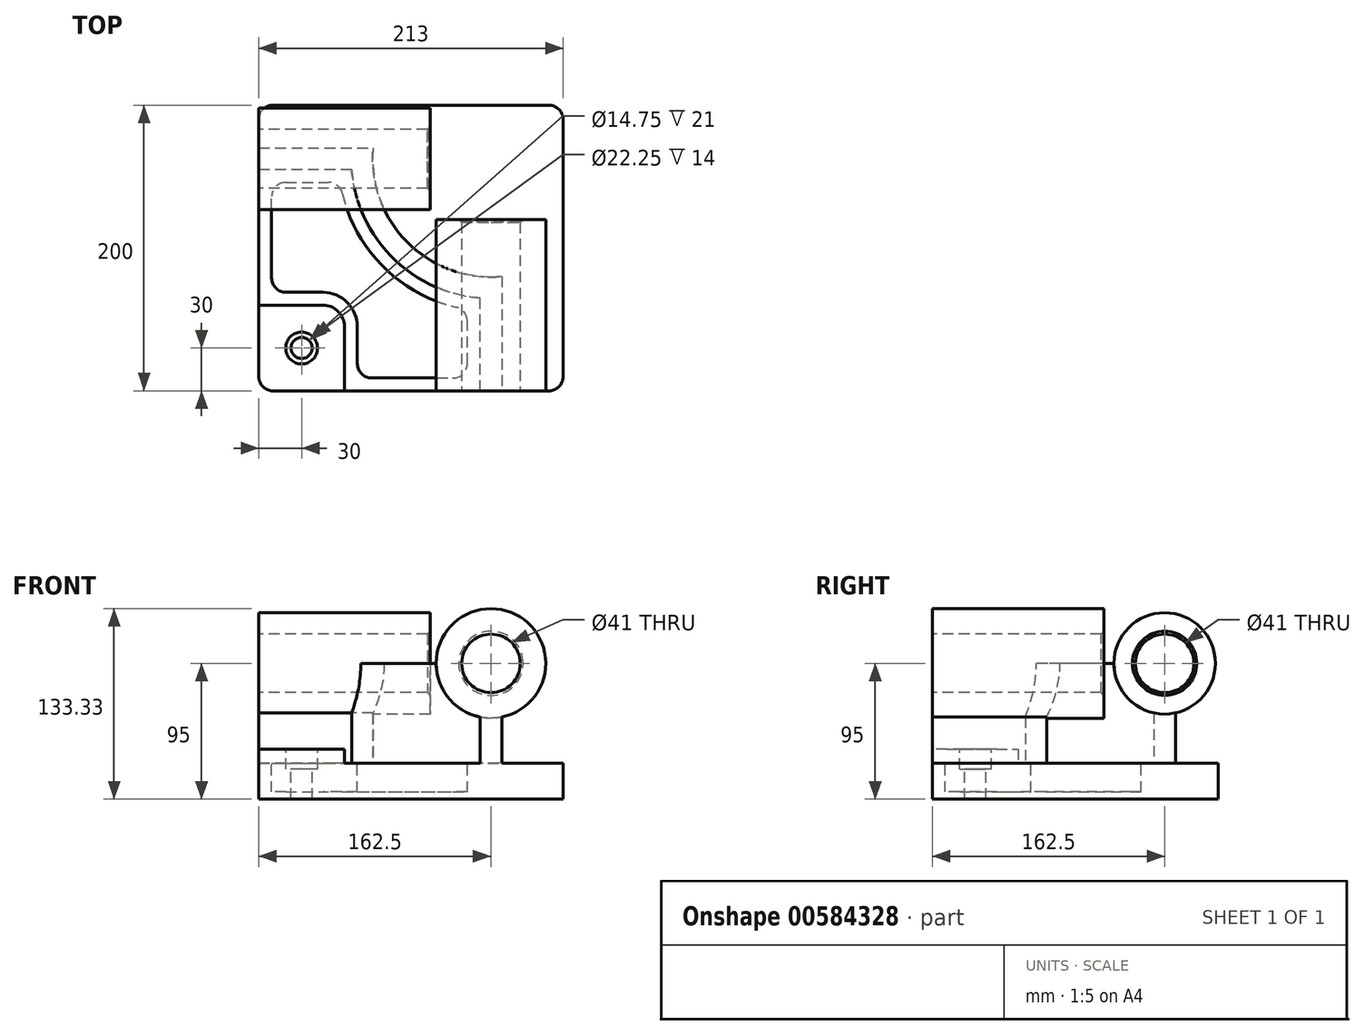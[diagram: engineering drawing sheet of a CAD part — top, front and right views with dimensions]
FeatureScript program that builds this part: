
annotation { "Feature Type Name" : "Feature", "Feature Type Description" : "" }
export const myFeature = defineFeature(function(context is Context, id is Id, definition is map)
    precondition{}
    {
        {
            var Q0;
            Q0=qCreatedBy(makeId("Front.planeOp"),FACE);
            var sketch = newSketch(context, id + "F0", { "sketchPlane" : qUnion([Q0])});
            skLineSegment(sketch, "E0.bottom", {"start": v(106.5, 0) * mm, "end": v(-106.5, 0) * mm});
            skLineSegment(sketch, "E0.top", {"start": v(106.5, 25) * mm, "end": v(-106.5, 25) * mm});
            skLineSegment(sketch, "E0.left", {"start": v(106.5, 0) * mm, "end": v(106.5, 25) * mm});
            skLineSegment(sketch, "E0.right", {"start": v(-106.5, 0) * mm, "end": v(-106.5, 25) * mm});
            skSolve(sketch);
        }
        {
            var Q0;
            Q0 = qSketchRegion(id + "F0", true);
            extrude(context, id + "F1", {"entities" : qUnion([Q0]), "endBound" : BoundingType.SYMMETRIC, "depth" : 200 * mm, "offsetDistance" : 25 * mm});
        }
        {
            var Q0;
            Q0=makeQuery(id+"F1.opExtrude","SWEPT_FACE",FACE,{"disambiguationData":[OSD([sQuery(id+"F0.wireOp",EDGE,"E0.top")])]});
            var sketch = newSketch(context, id + "F2", { "sketchPlane" : qUnion([Q0])});
            skLineSegment(sketch, "E1", {"start": v(-106.5, 70) * mm, "end": v(-26.5, 70) * mm});
            skLineSegment(sketch, "E2", {"start": v(-41.5, 55) * mm, "end": v(-106.5, 55) * mm});
            skLineSegment(sketch, "E3", {"start": v(-106.5, 55) * mm, "end": v(-106.5, 70) * mm});
            skLineSegment(sketch, "E4", {"start": v(48.5, -100) * mm, "end": v(48.5, -35) * mm});
            skLineSegment(sketch, "E5", {"start": v(63.5, -20) * mm, "end": v(63.5, -100) * mm});
            skLineSegment(sketch, "E6", {"start": v(63.5, -100) * mm, "end": v(48.5, -100) * mm});
            skLineSegment(sketch, "E7.0", {"start": v(106.5, -100) * mm, "end": v(106.5, 100) * mm});
            skArc(sketch, "E8", {"start": v(-26.5, 70) * mm, "mid": v(-2.47, 4.03) * mm, "end": v(63.5, -20) * mm});
            skArc(sketch, "E9", {"start": v(-41.5, 55) * mm, "mid": v(-13.07, -6.57) * mm, "end": v(48.5, -35) * mm});
            skLineSegment(sketch, "E10", {"start": v(-106.5, -40) * mm, "end": v(-61.5, -40) * mm});
            skLineSegment(sketch, "E11", {"start": v(-46.5, -55) * mm, "end": v(-46.5, -100) * mm});
            skLineSegment(sketch, "E12", {"start": v(-46.5, -100) * mm, "end": v(-106.5, -100) * mm});
            skLineSegment(sketch, "E13", {"start": v(-106.5, -100) * mm, "end": v(-106.5, -40) * mm});
            skLineSegment(sketch, "E14", {"start": v(-87.5, -31) * mm, "end": v(-61.5, -31) * mm});
            skLineSegment(sketch, "E15", {"start": v(-37.5, -55) * mm, "end": v(-37.5, -81) * mm});
            skLineSegment(sketch, "E16", {"start": v(-27.5, -91) * mm, "end": v(29.5, -91) * mm});
            skLineSegment(sketch, "E17", {"start": v(39.5, -81) * mm, "end": v(39.5, -51.2) * mm});
            skLineSegment(sketch, "E18", {"start": v(-97.5, -21) * mm, "end": v(-97.5, 36) * mm});
            skLineSegment(sketch, "E19", {"start": v(-87.5, 46) * mm, "end": v(-57.7, 46) * mm});
            skArc(sketch, "E20", {"start": v(-47.97, 38.29) * mm, "mid": v(-19.44, -12.94) * mm, "end": v(31.79, -41.47) * mm});
            skPoint(sketch, "E21.visualSharp", {"position": v(-46.5, -40) * mm});
            skArc(sketch, "E21.filletArc", {"start": v(-46.5, -55) * mm, "mid": v(-50.9, -44.4) * mm, "end": v(-61.5, -40) * mm});
            skPoint(sketch, "E22.visualSharp", {"position": v(-37.5, -31) * mm});
            skArc(sketch, "E22.filletArc", {"start": v(-37.5, -55) * mm, "mid": v(-44.53, -38.03) * mm, "end": v(-61.5, -31) * mm});
            skPoint(sketch, "E23.visualSharp", {"position": v(-97.5, -31) * mm});
            skArc(sketch, "E23.filletArc", {"start": v(-97.5, -21) * mm, "mid": v(-94.57, -28.07) * mm, "end": v(-87.5, -31) * mm});
            skPoint(sketch, "E24.visualSharp", {"position": v(-97.5, 46) * mm});
            skArc(sketch, "E24.filletArc", {"start": v(-87.5, 46) * mm, "mid": v(-94.57, 43.07) * mm, "end": v(-97.5, 36) * mm});
            skPoint(sketch, "E25.visualSharp", {"position": v(-49.48, 46) * mm});
            skArc(sketch, "E25.filletArc", {"start": v(-47.97, 38.29) * mm, "mid": v(-51.5, 43.84) * mm, "end": v(-57.7, 46) * mm});
            skPoint(sketch, "E26.visualSharp", {"position": v(39.5, -42.98) * mm});
            skArc(sketch, "E26.filletArc", {"start": v(39.5, -51.2) * mm, "mid": v(37.34, -45) * mm, "end": v(31.79, -41.47) * mm});
            skPoint(sketch, "E27.visualSharp", {"position": v(39.5, -91) * mm});
            skArc(sketch, "E27.filletArc", {"start": v(29.5, -91) * mm, "mid": v(36.57, -88.07) * mm, "end": v(39.5, -81) * mm});
            skPoint(sketch, "E28.visualSharp", {"position": v(-37.5, -91) * mm});
            skArc(sketch, "E28.filletArc", {"start": v(-37.5, -81) * mm, "mid": v(-34.57, -88.07) * mm, "end": v(-27.5, -91) * mm});
            skPoint(sketch, "E29.startSnap0", {"position": v(-2.47, 4.03) * mm});
            skPoint(sketch, "E30", {"position": v(63.5, -60) * mm});
            skSolve(sketch);
        }
        {
            var Q0;
            Q0=makeQuery(id+"F2.imprint","IMPRINT",FACE,{"disambiguationData":[TD([[makeQuery(id+"F2.imprint","IMPRINT",EDGE,{"derivedFrom":sQuery(id+"F2.wireOp",EDGE,"E14")}),1.0]])]});
            extrude(context, id + "F3", {"entities" : qUnion([Q0]), "operationType" : NewBodyOperationType.REMOVE, "oppositeDirection" : true, "depth" : 20 * mm, "offsetDistance" : 25 * mm});
        }
        {
            var Q0;
            Q0=makeQuery(id+"F2.imprint","IMPRINT",FACE,{"disambiguationData":[TD([[makeQuery(id+"F2.imprint","IMPRINT",EDGE,{"derivedFrom":sQuery(id+"F2.wireOp",EDGE,"E1")}),-1.0]])]});
            extrude(context, id + "F4", {"entities" : qUnion([Q0]), "operationType" : NewBodyOperationType.ADD, "depth" : 70 * mm, "offsetDistance" : 25 * mm});
        }
        {
            var Q0;
            Q0=makeQuery(id+"F4.boolean.opBoolean","MERGE",FACE,{"derivedFrom":[makeQuery(id+"F1.opExtrude","CAP_FACE",FACE,{"disambiguationData":[OSD([sQuery(id+"F0.wireOp",EDGE,"E0.bottom"),sQuery(id+"F0.wireOp",EDGE,"E0.top"),sQuery(id+"F0.wireOp",EDGE,"E0.left"),sQuery(id+"F0.wireOp",EDGE,"E0.right")])],"isStart":false}),makeQuery(id+"F4.opExtrude","SWEPT_FACE",FACE,{"disambiguationData":[OSD([sQuery(id+"F2.wireOp",EDGE,"E6")])]})]});
            var sketch = newSketch(context, id + "F5", { "sketchPlane" : qUnion([Q0])});
            skCircle(sketch, "E31", {"center": v(56, 95) * mm, "radius": 38.33 * mm});
            skCircle(sketch, "E32", {"center": v(56, 95) * mm, "radius": 20.5 * mm});
            skPoint(sketch, "E33.orphan", {"position": v(48.5, 95) * mm});
            skPoint(sketch, "E34.0.2.end.orphan", {"position": v(63.5, 95) * mm});
            skPoint(sketch, "E34.0.1.end.orphan", {"position": v(63.5, 25) * mm});
            skPoint(sketch, "E34.0.0.end.orphan", {"position": v(106.5, 25) * mm});
            skPoint(sketch, "E34.0.7.end.orphan", {"position": v(106.5, 0) * mm});
            skPoint(sketch, "E34.0.6.end.orphan", {"position": v(-106.5, 0) * mm});
            skPoint(sketch, "E34.0.5.end.orphan", {"position": v(-106.5, 25) * mm});
            skPoint(sketch, "E34.0.5.start.orphan", {"position": v(48.5, 25) * mm});
            skSolve(sketch);
        }
        {
            var Q0;
            Q0 = qSketchRegion(id + "F5", true);
            extrude(context, id + "F6", {"entities" : qUnion([Q0]), "operationType" : NewBodyOperationType.ADD, "oppositeDirection" : true, "depth" : 120 * mm, "offsetDistance" : 25 * mm});
        }
        {
            var Q0;
            Q0=makeQuery(id+"F4.boolean.opBoolean","MERGE",FACE,{"derivedFrom":[makeQuery(id+"F1.opExtrude","SWEPT_FACE",FACE,{"disambiguationData":[OSD([sQuery(id+"F0.wireOp",EDGE,"E0.right")])]}),makeQuery(id+"F4.opExtrude","SWEPT_FACE",FACE,{"disambiguationData":[OSD([sQuery(id+"F2.wireOp",EDGE,"E3")])]})]});
            var sketch = newSketch(context, id + "F7", { "sketchPlane" : qUnion([Q0])});
            skCircle(sketch, "E35", {"center": v(-62.5, 95) * mm, "radius": 35.5 * mm});
            skCircle(sketch, "E36", {"center": v(-62.5, 95) * mm, "radius": 20.5 * mm});
            skSolve(sketch);
        }
        {
            var Q0;
            Q0 = qSketchRegion(id + "F7", true);
            extrude(context, id + "F8", {"entities" : qUnion([Q0]), "operationType" : NewBodyOperationType.ADD, "oppositeDirection" : true, "depth" : 120 * mm, "offsetDistance" : 25 * mm});
        }
        {
            var Q0;
            {var subQ1=sQuery(id+"F2.wireOp",EDGE,"E3");var subQ8=makeQuery(id+"F4.opExtrude","CAP_EDGE",EDGE,{"disambiguationData":[OSD([subQ1])],"isStart":false});Q0=makeQuery(id+"F7.imprint","IMPRINT",FACE,{"disambiguationData":[TD([[makeQuery(id+"F7.imprint","IMPRINT",EDGE,{"derivedFrom":subQ8}),-1.0]])]});}
            var Q1;
            {var subQ1=sQuery(id+"F2.wireOp",EDGE,"E3");var subQ8=makeQuery(id+"F4.opExtrude","CAP_EDGE",EDGE,{"disambiguationData":[OSD([subQ1])],"isStart":false});Q1=makeQuery(id+"F7.imprint","IMPRINT",FACE,{"disambiguationData":[TD([[makeQuery(id+"F7.imprint","IMPRINT",EDGE,{"derivedFrom":subQ8}),1.0]])]});}
            extrude(context, id + "F9", {"entities" : qUnion([Q0, Q1]), "operationType" : NewBodyOperationType.REMOVE, "endBound" : BoundingType.THROUGH_ALL, "oppositeDirection" : true, "depth" : 25 * mm, "offsetDistance" : 25 * mm});
        }
        {
            var Q0;
            {var subQ1=sQuery(id+"F2.wireOp",EDGE,"E6");var subQ7=makeQuery(id+"F4.opExtrude","CAP_EDGE",EDGE,{"disambiguationData":[OSD([subQ1])],"isStart":false});Q0=makeQuery(id+"F5.imprint","IMPRINT",FACE,{"disambiguationData":[TD([[makeQuery(id+"F5.imprint","IMPRINT",EDGE,{"derivedFrom":subQ7}),-1.0]])]});}
            var Q1;
            {var subQ1=sQuery(id+"F2.wireOp",EDGE,"E6");var subQ7=makeQuery(id+"F4.opExtrude","CAP_EDGE",EDGE,{"disambiguationData":[OSD([subQ1])],"isStart":false});Q1=makeQuery(id+"F5.imprint","IMPRINT",FACE,{"disambiguationData":[TD([[makeQuery(id+"F5.imprint","IMPRINT",EDGE,{"derivedFrom":subQ7}),1.0]])]});}
            extrude(context, id + "F10", {"entities" : qUnion([Q0, Q1]), "operationType" : NewBodyOperationType.REMOVE, "endBound" : BoundingType.THROUGH_ALL, "oppositeDirection" : true, "depth" : 25 * mm, "offsetDistance" : 25 * mm});
        }
        {
            var Q0;
            Q0=makeQuery(id+"F2.imprint","IMPRINT",FACE,{"disambiguationData":[TD([[makeQuery(id+"F2.imprint","IMPRINT",EDGE,{"derivedFrom":sQuery(id+"F2.wireOp",EDGE,"E10")}),-1.0]])]});
            extrude(context, id + "F11", {"entities" : qUnion([Q0]), "operationType" : NewBodyOperationType.ADD, "depth" : 10 * mm, "offsetDistance" : 25 * mm});
        }
        {
            var Q0;
            Q0=makeQuery(id+"F11.opExtrude","CAP_FACE",FACE,{"disambiguationData":[OSD([sQuery(id+"F2.wireOp",EDGE,"E10"),sQuery(id+"F2.wireOp",EDGE,"E11"),sQuery(id+"F2.wireOp",EDGE,"E12"),sQuery(id+"F2.wireOp",EDGE,"E13"),sQuery(id+"F2.wireOp",EDGE,"E21.filletArc")])],"isStart":false});
            var sketch = newSketch(context, id + "F12", { "sketchPlane" : qUnion([Q0])});
            skPoint(sketch, "E37", {"position": v(-76.5, -70) * mm});
            skSolve(sketch);
        }
        {
            var Q0;
            Q0=sQuery(id+"F12.wireOp",VERTEX,"E37");
            var Q1;
            Q1=makeQuery(id+"F1.opExtrude","SWEPT_BODY",BODY,{"disambiguationData":[OSD([sQuery(id+"F0.wireOp",EDGE,"E0.bottom"),sQuery(id+"F0.wireOp",EDGE,"E0.top"),sQuery(id+"F0.wireOp",EDGE,"E0.left"),sQuery(id+"F0.wireOp",EDGE,"E0.right")])]});
            hole(context, id + "F13", {"style" : HoleStyle.C_BORE, "endStyle" : HoleEndStyle.THROUGH, "standardTappedOrClearance" : lookupTablePath({ "standard" : "ISO", "fit" : "Close", "size" : "M14", "type" : "Clearance" }), "standardBlindInLast" : lookupTablePath({ "fit" : "Close", "standard" : "ISO", "size" : "M14", "type" : "Clearance" }), "holeDiameter" : 14.75 * mm, "cBoreDiameter" : 22.25 * mm, "cBoreDepth" : 14 * mm, "majorDiameter" : 5 * mm, "isTappedThrough" : true, "tappedDepth" : 12 * mm, "tapClearance" : 3, "locations" : qUnion([Q0]), "scope" : qUnion([Q1])});
        }
        {
            var Q0;
            Q0=makeQuery(id+"F1.opExtrude","CAP_EDGE",EDGE,{"disambiguationData":[OSD([sQuery(id+"F0.wireOp",EDGE,"E0.left")])],"isStart":false});
            var Q1;
            Q1=makeQuery(id+"F1.opExtrude","CAP_EDGE",EDGE,{"disambiguationData":[OSD([sQuery(id+"F0.wireOp",EDGE,"E0.left")])],"isStart":true});
            var Q2;
            Q2=makeQuery(id+"F1.opExtrude","CAP_EDGE",EDGE,{"disambiguationData":[OSD([sQuery(id+"F0.wireOp",EDGE,"E0.right")])],"isStart":true});
            var Q3;
            Q3=makeQuery(id+"F11.boolean.opBoolean","MERGE",EDGE,{"derivedFrom":[makeQuery(id+"F1.opExtrude","CAP_EDGE",EDGE,{"disambiguationData":[OSD([sQuery(id+"F0.wireOp",EDGE,"E0.right")])],"isStart":false}),makeQuery(id+"F11.opExtrude","SWEPT_EDGE",EDGE,{"disambiguationData":[OSD([sQuery(id+"F2.wireOp",EDGE,"E12"),sQuery(id+"F2.wireOp",EDGE,"E13")])]})]});
            fillet(context, id + "F14", {"entities" : qUnion([Q0, Q1, Q2, Q3]), "radius" : 10 * mm, "tangentPropagation" : true, "allowEdgeOverflow" : false});
        }
        {
            var Q0;
            {var subQ0=sQuery(id+"F5.wireOp",EDGE,"E32");Q0=makeQuery(id+"F10.boolean.opBoolean","MERGE",EDGE,{"derivedFrom":[makeQuery(id+"F6.opExtrude","CAP_EDGE",EDGE,{"disambiguationData":[OSD([subQ0])],"isStart":true}),makeQuery(id+"F10.opExtrude","CAP_EDGE",EDGE,{"disambiguationData":[OSD([subQ0])],"isStart":true})]});}
            var Q1;
            {var subQ0=sQuery(id+"F7.wireOp",EDGE,"E36");Q1=makeQuery(id+"F9.boolean.opBoolean","MERGE",EDGE,{"derivedFrom":[makeQuery(id+"F8.opExtrude","CAP_EDGE",EDGE,{"disambiguationData":[OSD([subQ0])],"isStart":true}),makeQuery(id+"F9.opExtrude","CAP_EDGE",EDGE,{"disambiguationData":[OSD([subQ0])],"isStart":true})]});}
            var Q2;
            Q2=makeQuery(id+"F8.opExtrude","CAP_EDGE",EDGE,{"disambiguationData":[OSD([sQuery(id+"F7.wireOp",EDGE,"E36")])],"isStart":false});
            var Q3;
            Q3=makeQuery(id+"F6.opExtrude","CAP_EDGE",EDGE,{"disambiguationData":[OSD([sQuery(id+"F5.wireOp",EDGE,"E32")])],"isStart":false});
            chamfer(context, id + "F15", {"entities" : qUnion([Q0, Q1, Q2, Q3]), "chamferType" : ChamferType.OFFSET_ANGLE, "width" : 2 * mm, "oppositeDirection" : false, "angle" : 45 * degree, "tangentPropagation" : true});
        }
    });
